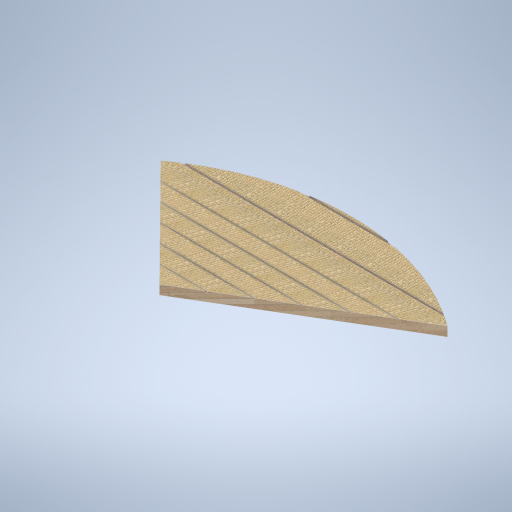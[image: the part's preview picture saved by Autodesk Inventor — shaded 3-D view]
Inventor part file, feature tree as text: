
AUTODESK INVENTOR PART (.ipt)
format: ipt  version: 2024.2 (Build 282272000, 272)  size: 434,688 bytes
history: native  units: mm
features: sketch x14, loft x6, plane x4, extrude x2
ambient origin geometry x8: Origin, YZ Plane, XZ Plane, XY Plane, X Axis, Y Axis, Z Axis, Center Point
bodies: Solid1 (feature_tree)
feature tree (26):
  sketch  "Sketch1"  dims[d0=90.0deg d1=90.0deg d2=100.0mm d3=0.0mm]
  plane  "Work Plane1"
  plane  "Work Plane2"
  plane  "Work Plane3"
  extrude  "Extrusion1"  Depth=100.0mm TaperAngle=0.0deg
  loft  "Loft1"
  loft  "Loft2"
  loft  "Loft3"
  loft  "Loft4"
  loft  "Loft5"
  loft  "Loft6"
  plane  "Work Plane4"
  extrude  "Extrusion2"  TaperAngle=0.0deg  [1 undecoded]
  sketch  "Sketch2"  dims[d4=1.745329mm d5=1.745329mm]
  sketch  "Sketch4"  dims[d6=0.0mm d7=90.0deg d8=0.0mm d9=90.0deg]
  sketch  "Sketch5"  dims[d12=0.0mm d13=90.0deg d14=0.0mm d15=90.0deg]
  sketch  "Sketch6"  dims[d18=0.0mm d19=90.0deg d20=0.0mm d21=90.0deg]
  sketch  "Sketch8"  dims[d24=0.0mm d25=90.0deg d26=0.0mm d27=90.0deg]
  sketch  "Sketch10"  dims[d30=0.0mm d31=90.0deg d32=0.0mm d33=90.0deg]
  sketch  "Sketch11"  dims[d36=0.0mm d37=90.0deg d38=0.0mm d39=90.0deg]
  sketch  "Sketch12"  dims[d40=135.0deg]
  sketch  "Sketch13"  dims[d41=3091.0mm d42=0.0mm]
  sketch  "Sketch14"
  sketch  "Sketch15"
  sketch  "Sketch16"
  sketch  "Sketch17"
note: 1 required parameter value undecoded (feature->parameter linkage not recoverable at this tier; creation-order binding heuristic only, values carry confidence <= 0.55)
